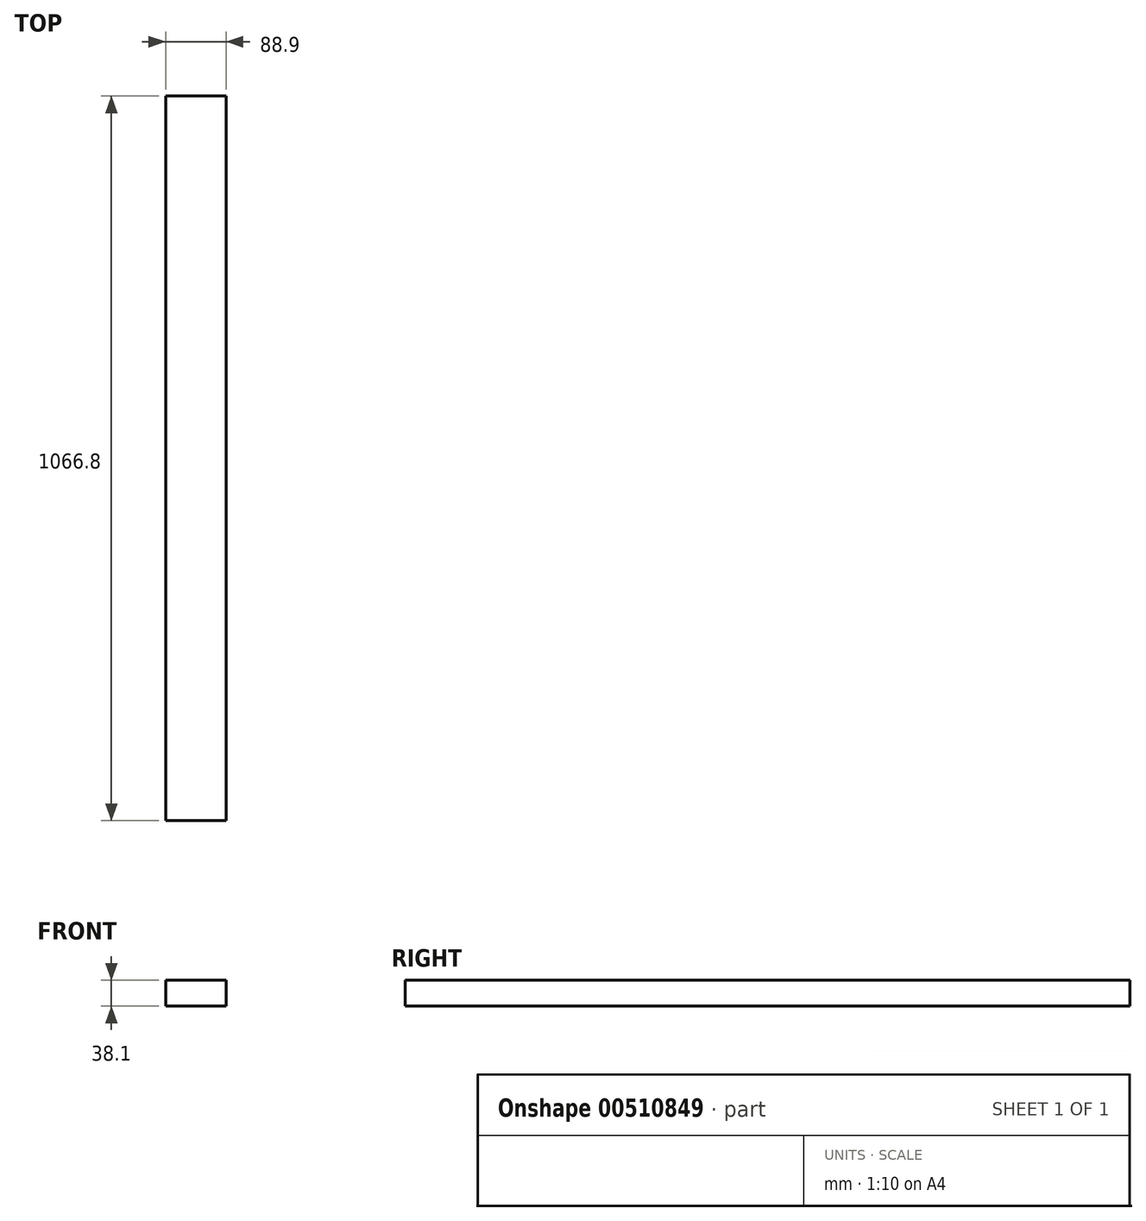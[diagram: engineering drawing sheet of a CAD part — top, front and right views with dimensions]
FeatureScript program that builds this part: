
annotation { "Feature Type Name" : "Feature", "Feature Type Description" : "" }
export const myFeature = defineFeature(function(context is Context, id is Id, definition is map)
    precondition{}
    {
        {
            var Q0;
            Q0=qCreatedBy(makeId("Front.planeOp"),FACE);
            var sketch = newSketch(context, id + "F0", { "sketchPlane" : qUnion([Q0])});
            skLineSegment(sketch, "E0", {"start": v(0, 19.05) * mm, "end": v(44.45, 19.05) * mm});
            skLineSegment(sketch, "E1", {"start": v(44.45, 19.05) * mm, "end": v(44.45, 0) * mm});
            skLineSegment(sketch, "E2.MirrorCS", {"start": v(-44.45, 19.05) * mm, "end": v(-44.45, 0) * mm});
            skLineSegment(sketch, "E3.MirrorCS", {"start": v(0, 19.05) * mm, "end": v(-44.45, 19.05) * mm});
            skLineSegment(sketch, "E4.MirrorCS", {"start": v(0, -19.05) * mm, "end": v(-44.45, -19.05) * mm});
            skLineSegment(sketch, "E5.MirrorCS", {"start": v(44.45, -19.05) * mm, "end": v(44.45, 0) * mm});
            skLineSegment(sketch, "E6.MirrorCS", {"start": v(0, -19.05) * mm, "end": v(44.45, -19.05) * mm});
            skLineSegment(sketch, "E7.MirrorCS", {"start": v(-44.45, -19.05) * mm, "end": v(-44.45, 0) * mm});
            skSolve(sketch);
        }
        {
            var Q0;
            Q0 = qSketchRegion(id + "F0", true);
            extrude(context, id + "F1", {"entities" : qUnion([Q0]), "depth" : 1066.8 * mm});
        }
    });
